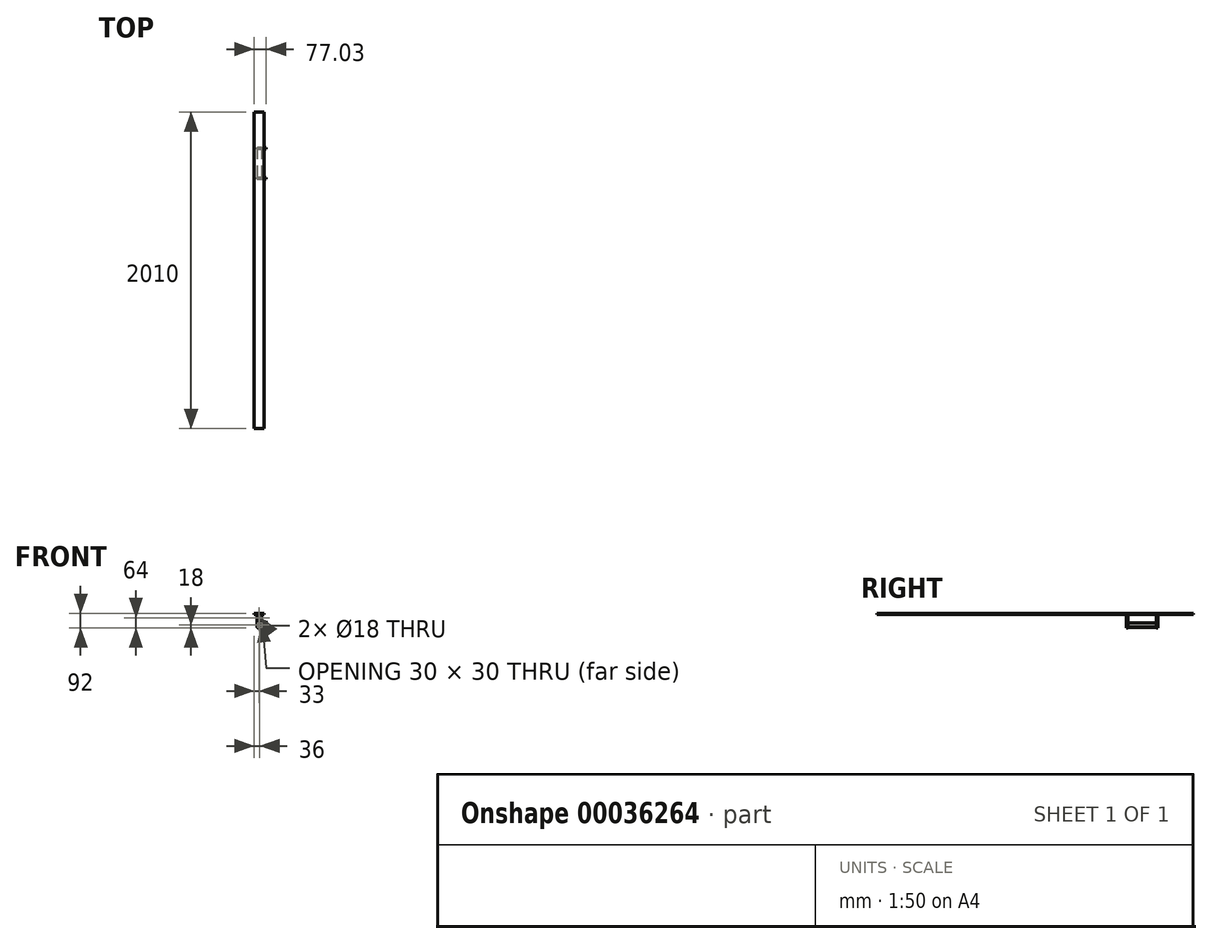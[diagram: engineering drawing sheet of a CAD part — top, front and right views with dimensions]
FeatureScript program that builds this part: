
annotation { "Feature Type Name" : "Feature", "Feature Type Description" : "" }
export const myFeature = defineFeature(function(context is Context, id is Id, definition is map)
    precondition{}
    {
        {
            var Q0;
            Q0=qCreatedBy(makeId("Front.planeOp"),FACE);
            var sketch = newSketch(context, id + "F0", { "sketchPlane" : qUnion([Q0])});
            skCircle(sketch, "E0", {"center": v(0, 0) * mm, "radius": 9 * mm});
            skLineSegment(sketch, "E1", {"start": v(-5, 15) * mm, "end": v(5, 15) * mm});
            skLineSegment(sketch, "E2", {"start": v(15, 5) * mm, "end": v(15, -38.46) * mm});
            skLineSegment(sketch, "E3", {"start": v(-15, 5) * mm, "end": v(-15, -54) * mm});
            skLineSegment(sketch, "E4", {"start": v(-5, -64) * mm, "end": v(44.03, -64) * mm});
            skLineSegment(sketch, "E5", {"start": v(44.03, -64) * mm, "end": v(44.03, -20) * mm});
            skLineSegment(sketch, "E6", {"start": v(44.03, -20) * mm, "end": v(19.96, -40.73) * mm});
            skPoint(sketch, "E7.visualSharp", {"position": v(15, -45) * mm});
            skArc(sketch, "E7.filletArc", {"start": v(15, -38.46) * mm, "mid": v(16.75, -41.18) * mm, "end": v(19.96, -40.73) * mm});
            skPoint(sketch, "E8.visualSharp", {"position": v(-15, -64) * mm});
            skArc(sketch, "E8.filletArc", {"start": v(-15, -54) * mm, "mid": v(-12.07, -61.07) * mm, "end": v(-5, -64) * mm});
            skPoint(sketch, "E9.visualSharp", {"position": v(-15, 15) * mm});
            skArc(sketch, "E9.filletArc", {"start": v(-5, 15) * mm, "mid": v(-12.07, 12.07) * mm, "end": v(-15, 5) * mm});
            skPoint(sketch, "E10.visualSharp", {"position": v(15, 15) * mm});
            skArc(sketch, "E10.filletArc", {"start": v(15, 5) * mm, "mid": v(12.07, 12.07) * mm, "end": v(5, 15) * mm});
            skSolve(sketch);
        }
        {
            var Q0;
            Q0 = qSketchRegion(id + "F0", true);
            extrude(context, id + "F1", {"entities" : qUnion([Q0]), "depth" : 10 * mm});
        }
        {
            var Q0;
            Q0=qCreatedBy(makeId("Front.planeOp"),FACE);
            cPlane(context, id + "F2", {"entities" : qUnion([Q0]), "cplaneType" : CPlaneType.OFFSET, "offset" : 220 * mm, "oppositeDirection" : true, "width" : 150 * mm, "height" : 150 * mm});
        }
        {
            var Q0;
            Q0=qCreatedBy(id+"F2.planeOp",FACE);
            cPlane(context, id + "F3", {"entities" : qUnion([Q0]), "cplaneType" : CPlaneType.OFFSET, "offset" : 5 * mm, "oppositeDirection" : true, "width" : 150 * mm, "height" : 150 * mm});
        }
        {
            var Q0;
            Q0=qCreatedBy(id+"F3.planeOp",FACE);
            var sketch = newSketch(context, id + "F4", { "sketchPlane" : qUnion([Q0])});
            skLineSegment(sketch, "E11", {"start": v(-33, 22) * mm, "end": v(32, 22) * mm});
            skLineSegment(sketch, "E12", {"start": v(32, 22) * mm, "end": v(32, 28) * mm});
            skLineSegment(sketch, "E13", {"start": v(32, 28) * mm, "end": v(-33, 28) * mm});
            skLineSegment(sketch, "E14", {"start": v(-33, 28) * mm, "end": v(-33, 22) * mm});
            skSolve(sketch);
        }
        {
            var Q0;
            Q0 = qSketchRegion(id + "F4", true);
            extrude(context, id + "F5", {"entities" : qUnion([Q0]), "operationType" : NewBodyOperationType.ADD, "depth" : 2010 * mm});
        }
        {
            var Q0;
            Q0=makeQuery(id+"F1.opExtrude","CAP_FACE",FACE,{"disambiguationData":[OSD([sQuery(id+"F0.wireOp",EDGE,"E0"),sQuery(id+"F0.wireOp",EDGE,"E1"),sQuery(id+"F0.wireOp",EDGE,"E2"),sQuery(id+"F0.wireOp",EDGE,"E3"),sQuery(id+"F0.wireOp",EDGE,"E4"),sQuery(id+"F0.wireOp",EDGE,"E5"),sQuery(id+"F0.wireOp",EDGE,"E6"),sQuery(id+"F0.wireOp",EDGE,"E7.filletArc"),sQuery(id+"F0.wireOp",EDGE,"E8.filletArc"),sQuery(id+"F0.wireOp",EDGE,"E9.filletArc"),sQuery(id+"F0.wireOp",EDGE,"E10.filletArc")])],"isStart":false});
            var sketch = newSketch(context, id + "F6", { "sketchPlane" : qUnion([Q0])});
            skLineSegment(sketch, "E15", {"start": v(18, -61) * mm, "end": v(-12, -61) * mm});
            skLineSegment(sketch, "E16", {"start": v(-12, -61) * mm, "end": v(-12, -31) * mm});
            skLineSegment(sketch, "E17.0", {"start": v(-9, -53) * mm, "end": v(-9, -33.5) * mm});
            skLineSegment(sketch, "E18.0", {"start": v(15.5, -58) * mm, "end": v(-4, -58) * mm});
            skLineSegment(sketch, "E19", {"start": v(18, -61) * mm, "end": v(18, -60.5) * mm});
            skLineSegment(sketch, "E20", {"start": v(-12, -31) * mm, "end": v(-11.5, -31) * mm});
            skArc(sketch, "E21.filletArc", {"start": v(-9, -53) * mm, "mid": v(-7.54, -56.54) * mm, "end": v(-4, -58) * mm});
            skPoint(sketch, "E22.visualSharp", {"position": v(18, -58) * mm});
            skArc(sketch, "E22.filletArc", {"start": v(18, -60.5) * mm, "mid": v(17.27, -58.73) * mm, "end": v(15.5, -58) * mm});
            skPoint(sketch, "E23.visualSharp", {"position": v(-9, -31) * mm});
            skArc(sketch, "E23.filletArc", {"start": v(-9, -33.5) * mm, "mid": v(-9.73, -31.73) * mm, "end": v(-11.5, -31) * mm});
            skSolve(sketch);
        }
        {
            var Q0;
            Q0 = qSketchRegion(id + "F6", true);
            extrude(context, id + "F7", {"entities" : qUnion([Q0]), "operationType" : NewBodyOperationType.ADD, "depth" : 180 * mm});
        }
        {
            var Q0;
            Q0=makeQuery(id+"F7.opExtrude","CAP_FACE",FACE,{"disambiguationData":[OSD([sQuery(id+"F6.wireOp",EDGE,"E15"),sQuery(id+"F6.wireOp",EDGE,"E16"),sQuery(id+"F6.wireOp",EDGE,"E17.0"),sQuery(id+"F6.wireOp",EDGE,"E18.0"),sQuery(id+"F6.wireOp",EDGE,"E19"),sQuery(id+"F6.wireOp",EDGE,"E20"),sQuery(id+"F6.wireOp",EDGE,"E21.filletArc"),sQuery(id+"F6.wireOp",EDGE,"E22.filletArc"),sQuery(id+"F6.wireOp",EDGE,"E23.filletArc")])],"isStart":false});
            var sketch = newSketch(context, id + "F8", { "sketchPlane" : qUnion([Q0])});
            skCircle(sketch, "E24", {"center": v(0, 0) * mm, "radius": 9 * mm});
            skLineSegment(sketch, "E25", {"start": v(-5, 15) * mm, "end": v(5, 15) * mm});
            skLineSegment(sketch, "E26", {"start": v(15, 5) * mm, "end": v(15, -38.46) * mm});
            skLineSegment(sketch, "E27", {"start": v(-15, 5) * mm, "end": v(-15, -54) * mm});
            skLineSegment(sketch, "E28", {"start": v(-5, -64) * mm, "end": v(44.03, -64) * mm});
            skLineSegment(sketch, "E29", {"start": v(44.03, -64) * mm, "end": v(44.03, -20) * mm});
            skLineSegment(sketch, "E30", {"start": v(44.03, -20) * mm, "end": v(19.96, -40.73) * mm});
            skPoint(sketch, "E31.visualSharp", {"position": v(15, -45) * mm});
            skArc(sketch, "E31.filletArc", {"start": v(15, -38.46) * mm, "mid": v(16.75, -41.18) * mm, "end": v(19.96, -40.73) * mm});
            skPoint(sketch, "E32.visualSharp", {"position": v(-15, -64) * mm});
            skArc(sketch, "E32.filletArc", {"start": v(-15, -54) * mm, "mid": v(-12.07, -61.07) * mm, "end": v(-5, -64) * mm});
            skPoint(sketch, "E33.visualSharp", {"position": v(-15, 15) * mm});
            skArc(sketch, "E33.filletArc", {"start": v(-5, 15) * mm, "mid": v(-12.07, 12.07) * mm, "end": v(-15, 5) * mm});
            skPoint(sketch, "E34.visualSharp", {"position": v(15, 15) * mm});
            skArc(sketch, "E34.filletArc", {"start": v(15, 5) * mm, "mid": v(12.07, 12.07) * mm, "end": v(5, 15) * mm});
            skSolve(sketch);
        }
        {
            var Q0;
            Q0 = qSketchRegion(id + "F8", true);
            extrude(context, id + "F9", {"entities" : qUnion([Q0]), "operationType" : NewBodyOperationType.ADD, "depth" : 10 * mm});
        }
    });
